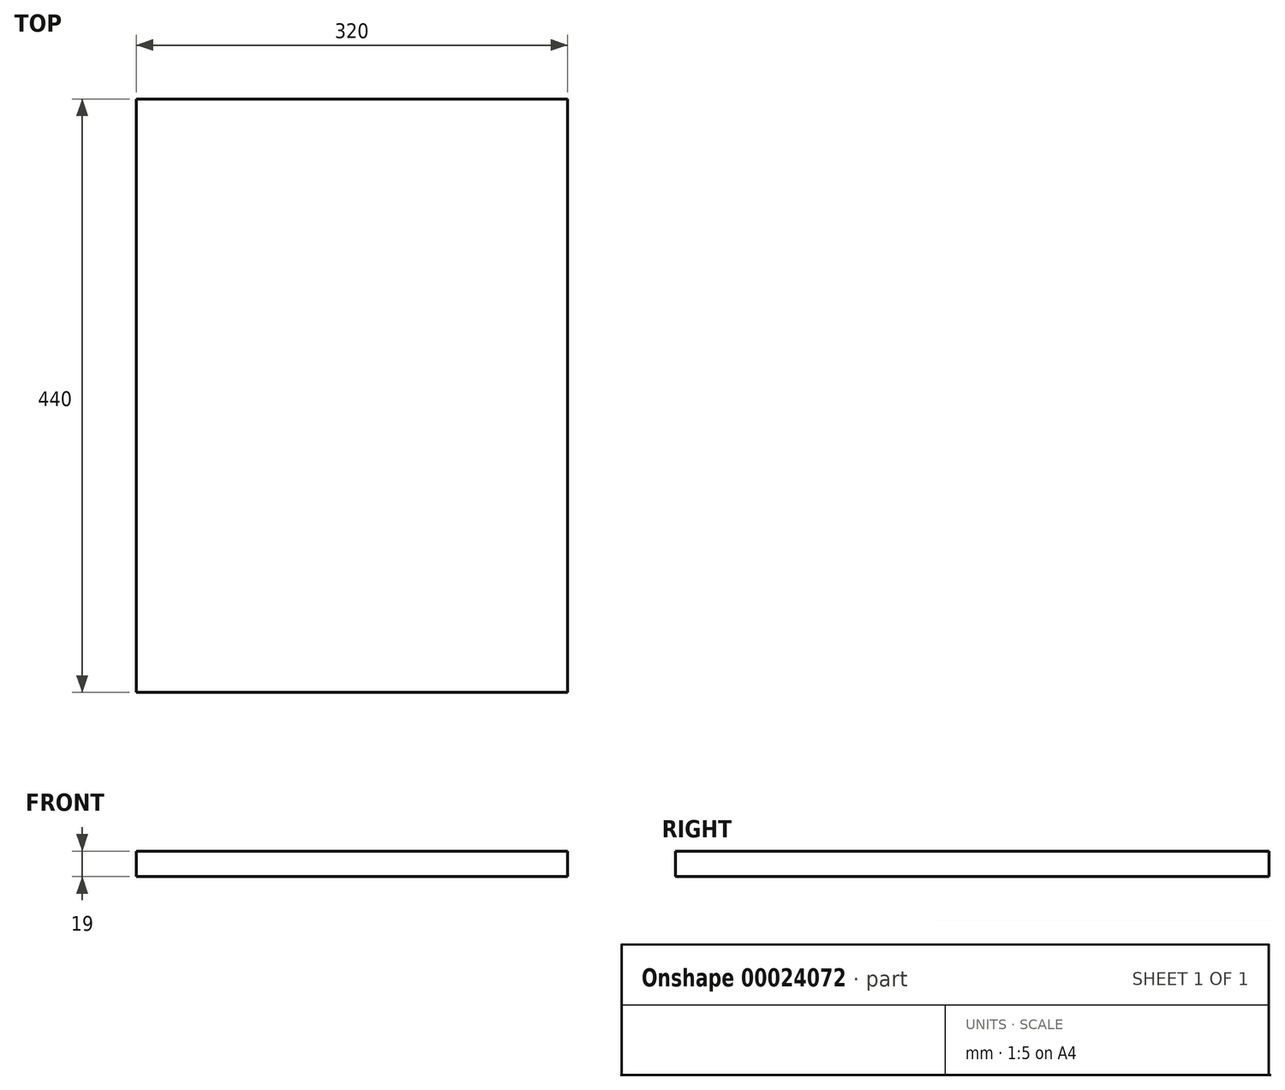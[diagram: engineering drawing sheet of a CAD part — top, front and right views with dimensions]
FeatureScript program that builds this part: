
annotation { "Feature Type Name" : "Feature", "Feature Type Description" : "" }
export const myFeature = defineFeature(function(context is Context, id is Id, definition is map)
    precondition{}
    {
        {
            var Q0;
            Q0=qCreatedBy(makeId("Top.planeOp"),FACE);
            var sketch = newSketch(context, id + "F0", { "sketchPlane" : qUnion([Q0])});
            skLineSegment(sketch, "E0.bottom", {"start": v(-70.96, 65.05) * mm, "end": v(249.04, 65.05) * mm});
            skLineSegment(sketch, "E0.top", {"start": v(-70.96, -374.95) * mm, "end": v(249.04, -374.95) * mm});
            skLineSegment(sketch, "E0.left", {"start": v(-70.96, 65.05) * mm, "end": v(-70.96, -374.95) * mm});
            skLineSegment(sketch, "E0.right", {"start": v(249.04, 65.05) * mm, "end": v(249.04, -374.95) * mm});
            skSolve(sketch);
        }
        {
            var Q0;
            Q0=qSketchRegion(id+"F0",true);
            extrude(context, id + "F1", {"entities" : qUnion([Q0]), "depth" : 19 * mm});
        }
    });
